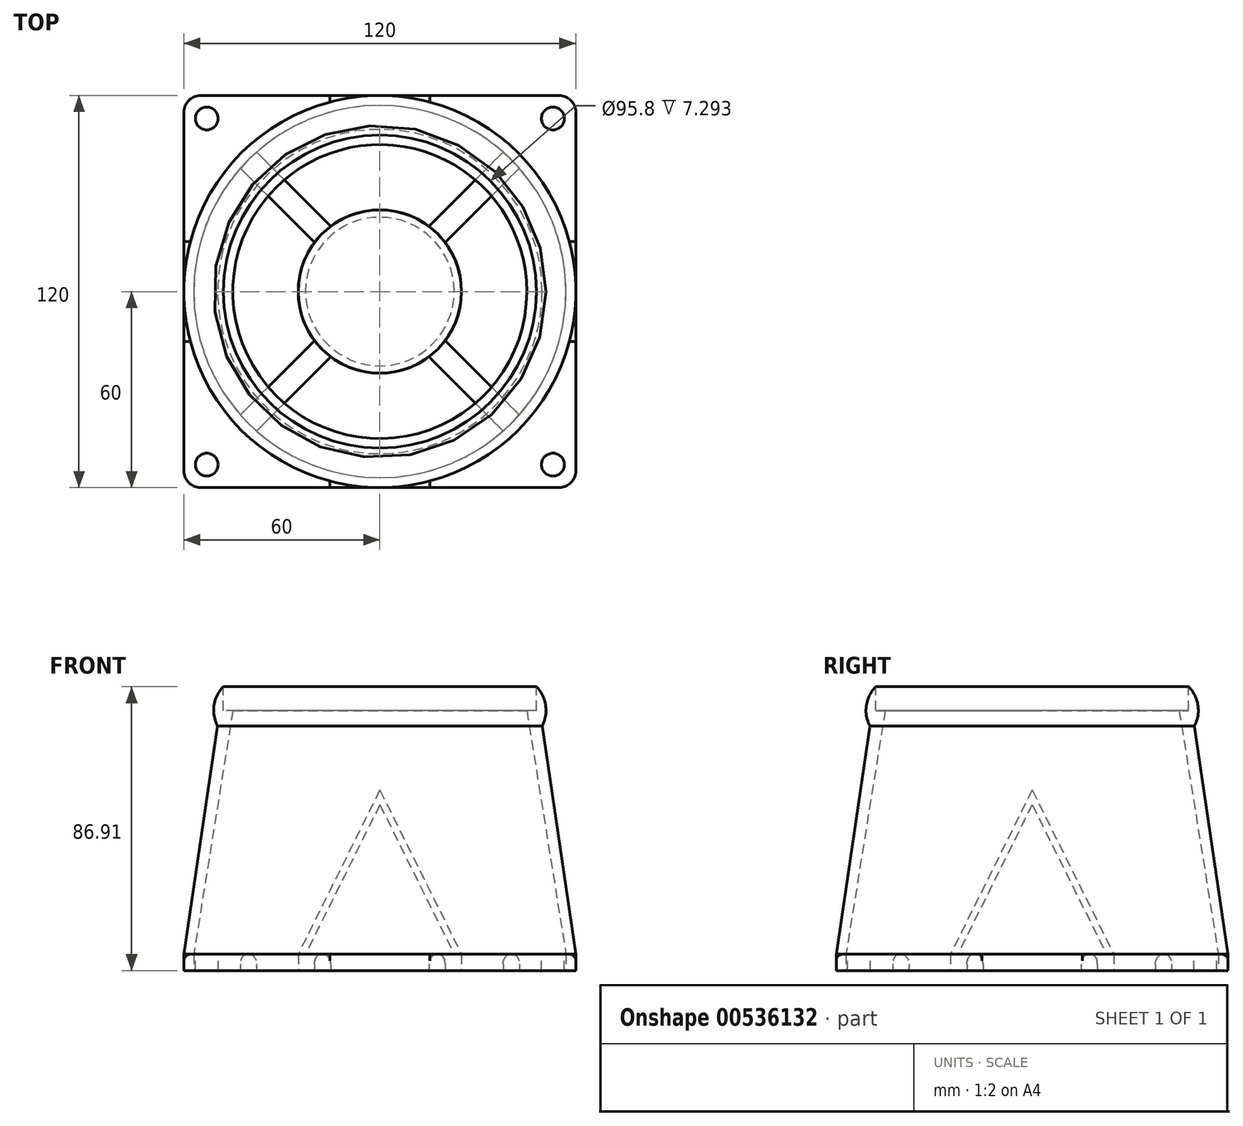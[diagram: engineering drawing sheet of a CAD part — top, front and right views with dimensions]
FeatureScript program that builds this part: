
annotation { "Feature Type Name" : "Feature", "Feature Type Description" : "" }
export const myFeature = defineFeature(function(context is Context, id is Id, definition is map)
    precondition{}
    {
        {
            var Q0;
            Q0=qCreatedBy(makeId("Top.planeOp"),FACE);
            var sketch = newSketch(context, id + "F0", { "sketchPlane" : qUnion([Q0])});
            skLineSegment(sketch, "E0.bottom", {"start": v(-60, 60) * mm, "end": v(60, 60) * mm});
            skLineSegment(sketch, "E0.top", {"start": v(-60, -60) * mm, "end": v(60, -60) * mm});
            skLineSegment(sketch, "E0.left", {"start": v(-60, 60) * mm, "end": v(-60, -60) * mm});
            skLineSegment(sketch, "E0.right", {"start": v(60, 60) * mm, "end": v(60, -60) * mm});
            skArc(sketch, "E1", {"start": v(37.75, 42.7) * mm, "mid": v(0, 57) * mm, "end": v(-37.75, 42.7) * mm});
            skArc(sketch, "E2", {"start": v(15.03, 19.98) * mm, "mid": v(0, 25) * mm, "end": v(-15.03, 19.98) * mm});
            skLineSegment(sketch, "E3", {"start": v(15.03, 19.98) * mm, "end": v(37.75, 42.7) * mm});
            skLineSegment(sketch, "E4", {"start": v(19.98, 15.03) * mm, "end": v(42.7, 37.75) * mm});
            skLineSegment(sketch, "E5.MirrorCS", {"start": v(15.03, -19.98) * mm, "end": v(37.75, -42.7) * mm});
            skLineSegment(sketch, "E6.MirrorCS", {"start": v(19.98, -15.03) * mm, "end": v(42.7, -37.75) * mm});
            skLineSegment(sketch, "E7.MirrorCS", {"start": v(-19.98, 15.03) * mm, "end": v(-42.7, 37.75) * mm});
            skLineSegment(sketch, "E8.MirrorCS", {"start": v(-19.98, -15.03) * mm, "end": v(-42.7, -37.75) * mm});
            skLineSegment(sketch, "E9.MirrorCS", {"start": v(-15.03, -19.98) * mm, "end": v(-37.75, -42.7) * mm});
            skLineSegment(sketch, "E10.MirrorCS", {"start": v(-15.03, 19.98) * mm, "end": v(-37.75, 42.7) * mm});
            skArc(sketch, "E11.trimOffspring", {"start": v(-42.7, 37.75) * mm, "mid": v(-57, 0) * mm, "end": v(-42.7, -37.75) * mm});
            skArc(sketch, "E12.trimOffspring", {"start": v(-19.98, 15.03) * mm, "mid": v(-25, 0) * mm, "end": v(-19.98, -15.03) * mm});
            skArc(sketch, "E13.trimOffspring", {"start": v(-15.03, -19.98) * mm, "mid": v(0, -25) * mm, "end": v(15.03, -19.98) * mm});
            skArc(sketch, "E14.trimOffspring", {"start": v(-37.75, -42.7) * mm, "mid": v(0, -57) * mm, "end": v(37.75, -42.7) * mm});
            skArc(sketch, "E15.trimOffspring", {"start": v(19.98, -15.03) * mm, "mid": v(25, 0) * mm, "end": v(19.98, 15.03) * mm});
            skArc(sketch, "E16.trimOffspring", {"start": v(42.7, -37.75) * mm, "mid": v(57, 0) * mm, "end": v(42.7, 37.75) * mm});
            skSolve(sketch);
        }
        {
            var Q0;
            Q0 = qSketchRegion(id + "F0", true);
            extrude(context, id + "F1", {"entities" : qUnion([Q0]), "depth" : 5 * mm, "offsetDistance" : 25.4 * mm});
        }
        {
            var Q0;
            Q0=makeQuery(id+"F1.opExtrude","CAP_FACE",FACE,{"disambiguationData":[OSD([sQuery(id+"F0.wireOp",EDGE,"E0.bottom"),sQuery(id+"F0.wireOp",EDGE,"E0.top"),sQuery(id+"F0.wireOp",EDGE,"E0.left"),sQuery(id+"F0.wireOp",EDGE,"E0.right"),sQuery(id+"F0.wireOp",EDGE,"E1"),sQuery(id+"F0.wireOp",EDGE,"E2"),sQuery(id+"F0.wireOp",EDGE,"E3"),sQuery(id+"F0.wireOp",EDGE,"E4"),sQuery(id+"F0.wireOp",EDGE,"E5.MirrorCS"),sQuery(id+"F0.wireOp",EDGE,"E6.MirrorCS"),sQuery(id+"F0.wireOp",EDGE,"E7.MirrorCS"),sQuery(id+"F0.wireOp",EDGE,"E8.MirrorCS"),sQuery(id+"F0.wireOp",EDGE,"E9.MirrorCS"),sQuery(id+"F0.wireOp",EDGE,"E10.MirrorCS"),sQuery(id+"F0.wireOp",EDGE,"E11.trimOffspring"),sQuery(id+"F0.wireOp",EDGE,"E12.trimOffspring"),sQuery(id+"F0.wireOp",EDGE,"E13.trimOffspring"),sQuery(id+"F0.wireOp",EDGE,"E14.trimOffspring"),sQuery(id+"F0.wireOp",EDGE,"E15.trimOffspring"),sQuery(id+"F0.wireOp",EDGE,"E16.trimOffspring")])],"isStart":false});
            var sketch = newSketch(context, id + "F2", { "sketchPlane" : qUnion([Q0])});
            skCircle(sketch, "E17", {"center": v(0, 0) * mm, "radius": 25 * mm});
            skPoint(sketch, "E18", {"position": v(53, -53) * mm});
            skPoint(sketch, "E19.MirrorP", {"position": v(53, 53) * mm});
            skPoint(sketch, "E20.MirrorP", {"position": v(-53, 53) * mm});
            skPoint(sketch, "E21.MirrorP", {"position": v(-53, -53) * mm});
            skSolve(sketch);
        }
        {
            var Q0;
            Q0=qCreatedBy(makeId("Right.planeOp"),FACE);
            var sketch = newSketch(context, id + "F3", { "sketchPlane" : qUnion([Q0])});
            skLineSegment(sketch, "E22", {"start": v(-22.75, 5.02) * mm, "end": v(-25, 5) * mm});
            skLineSegment(sketch, "E23", {"start": v(-25, 5) * mm, "end": v(0, 55.26) * mm});
            skLineSegment(sketch, "E24", {"start": v(0, 50.77) * mm, "end": v(0, 55.26) * mm});
            skLineSegment(sketch, "E25", {"start": v(0, 50.77) * mm, "end": v(-22.75, 5.02) * mm});
            skPoint(sketch, "E26.orphan", {"position": v(0, 5.26) * mm});
            skSolve(sketch);
        }
        {
            var Q0;
            Q0=makeQuery(id+"F3.imprint","IMPRINT",FACE,{"disambiguationData":[TD([[makeQuery(id+"F3.imprint","IMPRINT",EDGE,{"derivedFrom":sQuery(id+"F3.wireOp",EDGE,"E22")}),-1.0]])]});
            var Q1;
            Q1=sQuery(id+"F3.wireOp",EDGE,"E24");
            revolve(context, id + "F4", {"operationType" : NewBodyOperationType.ADD, "entities" : qUnion([Q0]), "axis" : qUnion([Q1]), "revolveType" : RevolveType.FULL});
        }
        {
            var Q0;
            Q0=makeQuery(id+"F1.opExtrude","CAP_EDGE",EDGE,{"disambiguationData":[OSD([sQuery(id+"F0.wireOp",EDGE,"E10.MirrorCS")])],"isStart":false});
            var Q1;
            Q1=makeQuery(id+"F1.opExtrude","CAP_EDGE",EDGE,{"disambiguationData":[OSD([sQuery(id+"F0.wireOp",EDGE,"E7.MirrorCS")])],"isStart":false});
            var Q2;
            Q2=makeQuery(id+"F1.opExtrude","CAP_EDGE",EDGE,{"disambiguationData":[OSD([sQuery(id+"F0.wireOp",EDGE,"E8.MirrorCS")])],"isStart":false});
            var Q3;
            Q3=makeQuery(id+"F1.opExtrude","CAP_EDGE",EDGE,{"disambiguationData":[OSD([sQuery(id+"F0.wireOp",EDGE,"E9.MirrorCS")])],"isStart":false});
            var Q4;
            Q4=makeQuery(id+"F1.opExtrude","CAP_EDGE",EDGE,{"disambiguationData":[OSD([sQuery(id+"F0.wireOp",EDGE,"E5.MirrorCS")])],"isStart":false});
            var Q5;
            Q5=makeQuery(id+"F1.opExtrude","CAP_EDGE",EDGE,{"disambiguationData":[OSD([sQuery(id+"F0.wireOp",EDGE,"E6.MirrorCS")])],"isStart":false});
            var Q6;
            Q6=makeQuery(id+"F1.opExtrude","CAP_EDGE",EDGE,{"disambiguationData":[OSD([sQuery(id+"F0.wireOp",EDGE,"E4")])],"isStart":false});
            var Q7;
            Q7=makeQuery(id+"F1.opExtrude","CAP_EDGE",EDGE,{"disambiguationData":[OSD([sQuery(id+"F0.wireOp",EDGE,"E3")])],"isStart":false});
            fillet(context, id + "F5", {"entities" : qUnion([Q0, Q1, Q2, Q3, Q4, Q5, Q6, Q7]), "radius" : 3 * mm, "tangentPropagation" : true, "allowEdgeOverflow" : false});
        }
        {
            var Q0;
            Q0=qCreatedBy(makeId("Right.planeOp"),FACE);
            var sketch = newSketch(context, id + "F6", { "sketchPlane" : qUnion([Q0])});
            skLineSegment(sketch, "E27", {"start": v(-57, 5) * mm, "end": v(-45, 79.62) * mm});
            skLineSegment(sketch, "E28", {"start": v(-60, 4.97) * mm, "end": v(-49.67, 74.9) * mm});
            skLineSegment(sketch, "E29", {"start": v(-45, 79.62) * mm, "end": v(-47.9, 79.62) * mm});
            skLineSegment(sketch, "E30", {"start": v(-47.9, 86.91) * mm, "end": v(-47.9, 79.62) * mm});
            skLineSegment(sketch, "E31", {"start": v(-57, 5) * mm, "end": v(-60, 4.97) * mm});
            skArc(sketch, "E32", {"start": v(-47.9, 86.91) * mm, "mid": v(-50.77, 81.2) * mm, "end": v(-49.67, 74.9) * mm});
            skSolve(sketch);
        }
        {
            var Q0;
            Q0=makeQuery(id+"F6.imprint","IMPRINT",FACE,{"disambiguationData":[TD([[makeQuery(id+"F6.imprint","IMPRINT",EDGE,{"derivedFrom":sQuery(id+"F6.wireOp",EDGE,"E27")}),1.0]])]});
            var Q1;
            Q1=makeQuery(id+"F4.opRevolve","SWEPT_FACE",FACE,{"disambiguationData":[OSD([sQuery(id+"F3.wireOp",EDGE,"E23")])]});
            revolve(context, id + "F7", {"operationType" : NewBodyOperationType.ADD, "entities" : qUnion([Q0]), "axis" : qUnion([Q1]), "revolveType" : RevolveType.FULL});
        }
        {
            var Q0;
            Q0=sQuery(id+"F2.wireOp",VERTEX,"E20.MirrorP");
            var Q1;
            Q1=sQuery(id+"F2.wireOp",VERTEX,"E19.MirrorP");
            var Q2;
            Q2=sQuery(id+"F2.wireOp",VERTEX,"E18");
            var Q3;
            Q3=sQuery(id+"F2.wireOp",VERTEX,"E21.MirrorP");
            var Q4;
            Q4=makeQuery(id+"F1.opExtrude","SWEPT_BODY",BODY,{"disambiguationData":[OSD([sQuery(id+"F0.wireOp",EDGE,"E0.bottom"),sQuery(id+"F0.wireOp",EDGE,"E0.top"),sQuery(id+"F0.wireOp",EDGE,"E0.left"),sQuery(id+"F0.wireOp",EDGE,"E0.right"),sQuery(id+"F0.wireOp",EDGE,"E1"),sQuery(id+"F0.wireOp",EDGE,"E2"),sQuery(id+"F0.wireOp",EDGE,"E3"),sQuery(id+"F0.wireOp",EDGE,"E4"),sQuery(id+"F0.wireOp",EDGE,"E5.MirrorCS"),sQuery(id+"F0.wireOp",EDGE,"E6.MirrorCS"),sQuery(id+"F0.wireOp",EDGE,"E7.MirrorCS"),sQuery(id+"F0.wireOp",EDGE,"E8.MirrorCS"),sQuery(id+"F0.wireOp",EDGE,"E9.MirrorCS"),sQuery(id+"F0.wireOp",EDGE,"E10.MirrorCS"),sQuery(id+"F0.wireOp",EDGE,"E11.trimOffspring"),sQuery(id+"F0.wireOp",EDGE,"E12.trimOffspring"),sQuery(id+"F0.wireOp",EDGE,"E13.trimOffspring"),sQuery(id+"F0.wireOp",EDGE,"E14.trimOffspring"),sQuery(id+"F0.wireOp",EDGE,"E15.trimOffspring"),sQuery(id+"F0.wireOp",EDGE,"E16.trimOffspring")])]});
            hole(context, id + "F8", {"style" : HoleStyle.SIMPLE, "endStyle" : HoleEndStyle.THROUGH, "holeDiameter" : 7 * mm, "isTappedThrough" : true, "tappedDepth" : 12.7 * mm, "tapClearance" : 3, "startFromSketch" : true, "locations" : qUnion([Q0, Q1, Q2, Q3]), "scope" : qUnion([Q4])});
        }
        {
            var Q0;
            Q0=makeQuery(id+"F1.opExtrude","SWEPT_EDGE",EDGE,{"disambiguationData":[OSD([sQuery(id+"F0.wireOp",EDGE,"E0.bottom"),sQuery(id+"F0.wireOp",EDGE,"E0.left")])]});
            var Q1;
            Q1=makeQuery(id+"F1.opExtrude","SWEPT_EDGE",EDGE,{"disambiguationData":[OSD([sQuery(id+"F0.wireOp",EDGE,"E0.bottom"),sQuery(id+"F0.wireOp",EDGE,"E0.right")])]});
            var Q2;
            Q2=makeQuery(id+"F1.opExtrude","SWEPT_EDGE",EDGE,{"disambiguationData":[OSD([sQuery(id+"F0.wireOp",EDGE,"E0.top"),sQuery(id+"F0.wireOp",EDGE,"E0.right")])]});
            var Q3;
            Q3=makeQuery(id+"F1.opExtrude","SWEPT_EDGE",EDGE,{"disambiguationData":[OSD([sQuery(id+"F0.wireOp",EDGE,"E0.top"),sQuery(id+"F0.wireOp",EDGE,"E0.left")])]});
            fillet(context, id + "F9", {"entities" : qUnion([Q0, Q1, Q2, Q3]), "radius" : 5.08 * mm, "tangentPropagation" : true, "allowEdgeOverflow" : false});
        }
        {
            var Q0;
            Q0=makeQuery(id+"F1.opExtrude","CAP_EDGE",EDGE,{"disambiguationData":[OSD([sQuery(id+"F0.wireOp",EDGE,"E0.bottom")])],"isStart":false});
            fillet(context, id + "F10", {"entities" : qUnion([Q0]), "radius" : 2 * mm, "tangentPropagation" : true, "allowEdgeOverflow" : false});
        }
    });
